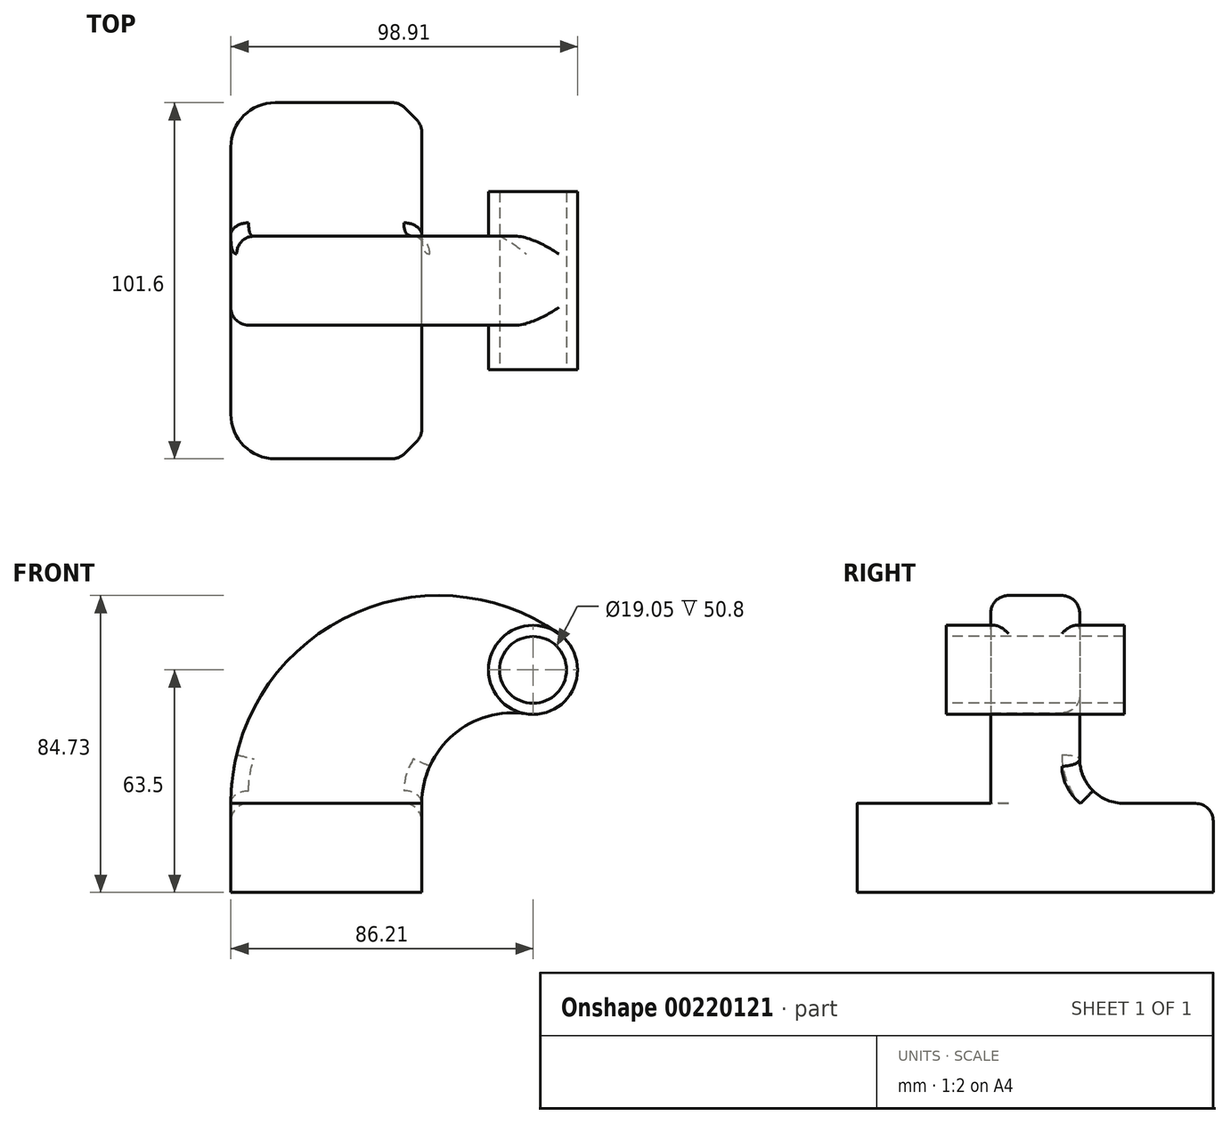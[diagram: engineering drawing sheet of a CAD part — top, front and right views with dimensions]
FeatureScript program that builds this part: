
annotation { "Feature Type Name" : "Feature", "Feature Type Description" : "" }
export const myFeature = defineFeature(function(context is Context, id is Id, definition is map)
    precondition{}
    {
        {
            var Q0;
            Q0=qCreatedBy(makeId("Front.planeOp"),FACE);
            var sketch = newSketch(context, id + "F0", { "sketchPlane" : qUnion([Q0])});
            skLineSegment(sketch, "E0.bottom", {"start": v(-54.46, 0) * mm, "end": v(0, 0) * mm});
            skLineSegment(sketch, "E0.top", {"start": v(-54.46, -25.4) * mm, "end": v(0, -25.4) * mm});
            skLineSegment(sketch, "E0.left", {"start": v(-54.46, 0) * mm, "end": v(-54.46, -25.4) * mm});
            skLineSegment(sketch, "E0.right", {"start": v(0, 0) * mm, "end": v(0, -25.4) * mm});
            skCircle(sketch, "E1", {"center": v(31.75, 38.1) * mm, "radius": 12.7 * mm});
            skArc(sketch, "E2", {"start": v(0, 0) * mm, "mid": v(9.03, 19.63) * mm, "end": v(29.8, 25.55) * mm});
            skArc(sketch, "E3", {"start": v(-54.46, 0) * mm, "mid": v(-22.43, 52.67) * mm, "end": v(39.07, 48.48) * mm});
            skLineSegment(sketch, "E4", {"start": v(39.07, 48.48) * mm, "end": v(39.07, 48.48) * mm});
            skSolve(sketch);
        }
        {
            var Q0;
            Q0=makeQuery(id+"F0.imprint","IMPRINT",FACE,{"disambiguationData":[TD([[makeQuery(id+"F0.imprint","IMPRINT",EDGE,{"derivedFrom":sQuery(id+"F0.wireOp",EDGE,"E0.bottom")}),-1.0]])]});
            extrude(context, id + "F1", {"entities" : qUnion([Q0]), "endBound" : BoundingType.SYMMETRIC, "depth" : 101.6 * mm});
        }
        {
            var Q0;
            Q0=makeQuery(id+"F0.imprint","IMPRINT",FACE,{"disambiguationData":[TD([[makeQuery(id+"F0.imprint","IMPRINT",EDGE,{"derivedFrom":sQuery(id+"F0.wireOp",EDGE,"E0.bottom")}),1.0]])]});
            extrude(context, id + "F2", {"entities" : qUnion([Q0]), "operationType" : NewBodyOperationType.ADD, "endBound" : BoundingType.SYMMETRIC, "depth" : 25.4 * mm});
        }
        {
            var Q0;
            {var subQ0=sQuery(id+"F0.wireOp",EDGE,"E1");var subQ1=makeQuery(id+"F0.imprint","INTERSECT",VERTEX,{"derivedFrom":[subQ0,sQuery(id+"F0.wireOp",EDGE,"E2")]});Q0=makeQuery(id+"F0.imprint","IMPRINT",FACE,{"disambiguationData":[TD([[makeQuery(id+"F0.imprint","IMPRINT",EDGE,{"disambiguationData":[TD([[subQ1,1.0]])],"derivedFrom":subQ0}),1.0]])]});}
            extrude(context, id + "F3", {"entities" : qUnion([Q0]), "operationType" : NewBodyOperationType.ADD, "endBound" : BoundingType.SYMMETRIC, "depth" : 50.8 * mm});
        }
        {
            var Q0;
            Q0=makeQuery(id+"F1.opExtrude","CAP_EDGE",EDGE,{"disambiguationData":[OSD([sQuery(id+"F0.wireOp",EDGE,"E0.right")])],"isStart":false});
            var Q1;
            Q1=makeQuery(id+"F1.opExtrude","CAP_EDGE",EDGE,{"disambiguationData":[OSD([sQuery(id+"F0.wireOp",EDGE,"E0.right")])],"isStart":true});
            chamfer(context, id + "F4", {"entities" : qUnion([Q0, Q1]), "width" : 6.35 * mm, "tangentPropagation" : true});
        }
        {
            var Q0;
            Q0=makeQuery(id+"F1.opExtrude","CAP_EDGE",EDGE,{"disambiguationData":[OSD([sQuery(id+"F0.wireOp",EDGE,"E0.left")])],"isStart":false});
            var Q1;
            Q1=makeQuery(id+"F1.opExtrude","CAP_EDGE",EDGE,{"disambiguationData":[OSD([sQuery(id+"F0.wireOp",EDGE,"E0.left")])],"isStart":true});
            fillet(context, id + "F5", {"entities" : qUnion([Q0, Q1]), "radius" : 12.7 * mm, "tangentPropagation" : true, "allowEdgeOverflow" : false});
        }
        {
            var Q0;
            Q0=makeQuery(id+"F2.opExtrude","CAP_EDGE",EDGE,{"disambiguationData":[OSD([sQuery(id+"F0.wireOp",EDGE,"E0.bottom")])],"isStart":false});
            var Q1;
            Q1=makeQuery(id+"F2.opExtrude","CAP_EDGE",EDGE,{"disambiguationData":[OSD([sQuery(id+"F0.wireOp",EDGE,"E0.bottom")])],"isStart":true});
            fillet(context, id + "F6", {"entities" : qUnion([Q0, Q1]), "radius" : 12.7 * mm, "tangentPropagation" : true, "allowEdgeOverflow" : false});
        }
        {
            var Q0;
            {var subQ0=sQuery(id+"F0.wireOp",EDGE,"E0.right");Q0=makeQuery(id+"F4.opChamfer","BLEND_EDGE",EDGE,{"blendedFrom":[makeQuery(id+"F1.opExtrude","CAP_EDGE",EDGE,{"disambiguationData":[OSD([subQ0])],"isStart":false}),makeQuery(id+"F1.opExtrude","SWEPT_FACE",FACE,{"disambiguationData":[OSD([subQ0])]})],"blendedInto":[makeQuery(id+"F1.opExtrude","SWEPT_FACE",FACE,{"disambiguationData":[OSD([subQ0])]})]});}
            var Q1;
            {var subQ0=sQuery(id+"F0.wireOp",EDGE,"E0.right");Q1=makeQuery(id+"F4.opChamfer","BLEND_EDGE",EDGE,{"blendedFrom":[makeQuery(id+"F1.opExtrude","CAP_EDGE",EDGE,{"disambiguationData":[OSD([subQ0])],"isStart":false}),makeQuery(id+"F1.opExtrude","CAP_FACE",FACE,{"disambiguationData":[OSD([sQuery(id+"F0.wireOp",EDGE,"E0.bottom"),sQuery(id+"F0.wireOp",EDGE,"E0.top"),sQuery(id+"F0.wireOp",EDGE,"E0.left"),subQ0])],"isStart":false})],"blendedInto":[makeQuery(id+"F1.opExtrude","CAP_FACE",FACE,{"disambiguationData":[OSD([sQuery(id+"F0.wireOp",EDGE,"E0.bottom"),sQuery(id+"F0.wireOp",EDGE,"E0.top"),sQuery(id+"F0.wireOp",EDGE,"E0.left"),subQ0])],"isStart":false})]});}
            var Q2;
            {var subQ0=sQuery(id+"F0.wireOp",EDGE,"E0.right");Q2=makeQuery(id+"F4.opChamfer","BLEND_EDGE",EDGE,{"blendedFrom":[makeQuery(id+"F1.opExtrude","CAP_EDGE",EDGE,{"disambiguationData":[OSD([subQ0])],"isStart":true}),makeQuery(id+"F1.opExtrude","SWEPT_FACE",FACE,{"disambiguationData":[OSD([subQ0])]})],"blendedInto":[makeQuery(id+"F1.opExtrude","SWEPT_FACE",FACE,{"disambiguationData":[OSD([subQ0])]})]});}
            var Q3;
            {var subQ0=sQuery(id+"F0.wireOp",EDGE,"E0.right");Q3=makeQuery(id+"F4.opChamfer","BLEND_EDGE",EDGE,{"blendedFrom":[makeQuery(id+"F1.opExtrude","CAP_EDGE",EDGE,{"disambiguationData":[OSD([subQ0])],"isStart":true}),makeQuery(id+"F1.opExtrude","CAP_FACE",FACE,{"disambiguationData":[OSD([sQuery(id+"F0.wireOp",EDGE,"E0.bottom"),sQuery(id+"F0.wireOp",EDGE,"E0.top"),sQuery(id+"F0.wireOp",EDGE,"E0.left"),subQ0])],"isStart":true})],"blendedInto":[makeQuery(id+"F1.opExtrude","CAP_FACE",FACE,{"disambiguationData":[OSD([sQuery(id+"F0.wireOp",EDGE,"E0.bottom"),sQuery(id+"F0.wireOp",EDGE,"E0.top"),sQuery(id+"F0.wireOp",EDGE,"E0.left"),subQ0])],"isStart":true})]});}
            fillet(context, id + "F7", {"entities" : qUnion([Q0, Q1, Q2, Q3]), "radius" : 5.08 * mm, "tangentPropagation" : true, "allowEdgeOverflow" : false});
        }
        {
            var Q0;
            Q0=makeQuery(id+"F2.opExtrude","CAP_EDGE",EDGE,{"disambiguationData":[OSD([sQuery(id+"F0.wireOp",EDGE,"E3")])],"isStart":true});
            var Q1;
            Q1=makeQuery(id+"F2.opExtrude","CAP_EDGE",EDGE,{"disambiguationData":[OSD([sQuery(id+"F0.wireOp",EDGE,"E2")])],"isStart":true});
            var Q2;
            Q2=makeQuery(id+"F6.opFillet","BLEND_EDGE",EDGE,{"blendedFrom":[makeQuery(id+"F2.opExtrude","CAP_EDGE",EDGE,{"disambiguationData":[OSD([sQuery(id+"F0.wireOp",EDGE,"E0.bottom")])],"isStart":true}),makeQuery(id+"F2.opExtrude","SWEPT_FACE",FACE,{"disambiguationData":[OSD([sQuery(id+"F0.wireOp",EDGE,"E2")])]})],"blendedInto":[makeQuery(id+"F2.opExtrude","SWEPT_FACE",FACE,{"disambiguationData":[OSD([sQuery(id+"F0.wireOp",EDGE,"E2")])]})]});
            var Q3;
            {var subQ2=sQuery(id+"F0.wireOp",EDGE,"E0.bottom");var subQ3=sQuery(id+"F0.wireOp",EDGE,"E0.right");var subQ4=sQuery(id+"F0.wireOp",EDGE,"E0.left");Q3=makeQuery(id+"F5.opFillet","BLEND_EDGE",EDGE,{"blendedFrom":[makeQuery(id+"F1.opExtrude","CAP_EDGE",EDGE,{"disambiguationData":[OSD([subQ4])],"isStart":true}),makeQuery(id+"F2.boolean.opBoolean","SPLIT",FACE,{"disambiguationData":[TD([makeQuery(id+"F1.opExtrude","CAP_FACE",FACE,{"disambiguationData":[OSD([subQ2,sQuery(id+"F0.wireOp",EDGE,"E0.top"),subQ4,subQ3])],"isStart":true})])],"derivedFrom":makeQuery(id+"F1.opExtrude","SWEPT_FACE",FACE,{"disambiguationData":[OSD([subQ2])]})})],"blendedInto":[makeQuery(id+"F2.boolean.opBoolean","SPLIT",FACE,{"disambiguationData":[TD([makeQuery(id+"F1.opExtrude","CAP_FACE",FACE,{"disambiguationData":[OSD([subQ2,sQuery(id+"F0.wireOp",EDGE,"E0.top"),subQ4,subQ3])],"isStart":true})])],"derivedFrom":makeQuery(id+"F1.opExtrude","SWEPT_FACE",FACE,{"disambiguationData":[OSD([subQ2])]})})]});}
            var Q4;
            Q4=makeQuery(id+"F1.opExtrude","CAP_EDGE",EDGE,{"disambiguationData":[OSD([sQuery(id+"F0.wireOp",EDGE,"E0.bottom")])],"isStart":true});
            var Q5;
            {var subQ0=sQuery(id+"F0.wireOp",EDGE,"E2");var subQ1=sQuery(id+"F0.wireOp",EDGE,"E0.bottom");var subQ2=sQuery(id+"F0.wireOp",EDGE,"E0.right");Q5=makeQuery(id+"F2.boolean.opBoolean","SPLIT",EDGE,{"disambiguationData":[TD([makeQuery(id+"F1.opExtrude","CAP_FACE",FACE,{"disambiguationData":[OSD([subQ1,sQuery(id+"F0.wireOp",EDGE,"E0.top"),sQuery(id+"F0.wireOp",EDGE,"E0.left"),subQ2])],"isStart":true})])],"derivedFrom":makeQuery(id+"F1.opExtrude","SWEPT_EDGE",EDGE,{"disambiguationData":[OSD([subQ1,subQ2,subQ0])]})});}
            var Q6;
            {var subQ2=sQuery(id+"F0.wireOp",EDGE,"E0.bottom");var subQ3=sQuery(id+"F0.wireOp",EDGE,"E0.right");var subQ4=sQuery(id+"F0.wireOp",EDGE,"E0.left");Q6=makeQuery(id+"F4.opChamfer","BLEND_EDGE",EDGE,{"blendedFrom":[makeQuery(id+"F1.opExtrude","CAP_EDGE",EDGE,{"disambiguationData":[OSD([subQ3])],"isStart":true}),makeQuery(id+"F2.boolean.opBoolean","SPLIT",FACE,{"disambiguationData":[TD([makeQuery(id+"F1.opExtrude","CAP_FACE",FACE,{"disambiguationData":[OSD([subQ2,sQuery(id+"F0.wireOp",EDGE,"E0.top"),subQ4,subQ3])],"isStart":true})])],"derivedFrom":makeQuery(id+"F1.opExtrude","SWEPT_FACE",FACE,{"disambiguationData":[OSD([subQ2])]})})],"blendedInto":[makeQuery(id+"F2.boolean.opBoolean","SPLIT",FACE,{"disambiguationData":[TD([makeQuery(id+"F1.opExtrude","CAP_FACE",FACE,{"disambiguationData":[OSD([subQ2,sQuery(id+"F0.wireOp",EDGE,"E0.top"),subQ4,subQ3])],"isStart":true})])],"derivedFrom":makeQuery(id+"F1.opExtrude","SWEPT_FACE",FACE,{"disambiguationData":[OSD([subQ2])]})})]});}
            var Q7;
            {var subQ2=sQuery(id+"F0.wireOp",EDGE,"E0.bottom");var subQ3=sQuery(id+"F0.wireOp",EDGE,"E0.right");var subQ4=sQuery(id+"F0.wireOp",EDGE,"E0.left");var subQ5=makeQuery(id+"F1.opExtrude","CAP_FACE",FACE,{"disambiguationData":[OSD([subQ2,sQuery(id+"F0.wireOp",EDGE,"E0.top"),subQ4,subQ3])],"isStart":true});Q7=makeQuery(id+"F7.opFillet","BLEND_EDGE",EDGE,{"blendedFrom":[makeQuery(id+"F4.opChamfer","BLEND_EDGE",EDGE,{"blendedFrom":[makeQuery(id+"F1.opExtrude","CAP_EDGE",EDGE,{"disambiguationData":[OSD([subQ3])],"isStart":true}),subQ5],"blendedInto":[subQ5]}),makeQuery(id+"F2.boolean.opBoolean","SPLIT",FACE,{"disambiguationData":[TD([subQ5])],"derivedFrom":makeQuery(id+"F1.opExtrude","SWEPT_FACE",FACE,{"disambiguationData":[OSD([subQ2])]})})],"blendedInto":[makeQuery(id+"F2.boolean.opBoolean","SPLIT",FACE,{"disambiguationData":[TD([subQ5])],"derivedFrom":makeQuery(id+"F1.opExtrude","SWEPT_FACE",FACE,{"disambiguationData":[OSD([subQ2])]})})]});}
            var Q8;
            {var subQ2=sQuery(id+"F0.wireOp",EDGE,"E0.bottom");var subQ3=sQuery(id+"F0.wireOp",EDGE,"E0.right");var subQ4=makeQuery(id+"F1.opExtrude","SWEPT_FACE",FACE,{"disambiguationData":[OSD([subQ3])]});var subQ5=sQuery(id+"F0.wireOp",EDGE,"E0.left");Q8=makeQuery(id+"F7.opFillet","BLEND_EDGE",EDGE,{"blendedFrom":[makeQuery(id+"F4.opChamfer","BLEND_EDGE",EDGE,{"blendedFrom":[makeQuery(id+"F1.opExtrude","CAP_EDGE",EDGE,{"disambiguationData":[OSD([subQ3])],"isStart":true}),subQ4],"blendedInto":[subQ4]}),makeQuery(id+"F2.boolean.opBoolean","SPLIT",FACE,{"disambiguationData":[TD([makeQuery(id+"F1.opExtrude","CAP_FACE",FACE,{"disambiguationData":[OSD([subQ2,sQuery(id+"F0.wireOp",EDGE,"E0.top"),subQ5,subQ3])],"isStart":true})])],"derivedFrom":makeQuery(id+"F1.opExtrude","SWEPT_FACE",FACE,{"disambiguationData":[OSD([subQ2])]})})],"blendedInto":[makeQuery(id+"F2.boolean.opBoolean","SPLIT",FACE,{"disambiguationData":[TD([makeQuery(id+"F1.opExtrude","CAP_FACE",FACE,{"disambiguationData":[OSD([subQ2,sQuery(id+"F0.wireOp",EDGE,"E0.top"),subQ5,subQ3])],"isStart":true})])],"derivedFrom":makeQuery(id+"F1.opExtrude","SWEPT_FACE",FACE,{"disambiguationData":[OSD([subQ2])]})})]});}
            var Q9;
            Q9=makeQuery(id+"F2.opExtrude","CAP_EDGE",EDGE,{"disambiguationData":[OSD([sQuery(id+"F0.wireOp",EDGE,"E3")])],"isStart":false});
            fillet(context, id + "F8", {"entities" : qUnion([Q0, Q1, Q2, Q3, Q4, Q5, Q6, Q7, Q8, Q9]), "radius" : 5.08 * mm, "tangentPropagation" : true, "allowEdgeOverflow" : false});
        }
        {
            var Q0;
            Q0=makeQuery(id+"F3.opExtrude","CAP_FACE",FACE,{"disambiguationData":[OSD([sQuery(id+"F0.wireOp",EDGE,"E1")])],"isStart":false});
            var sketch = newSketch(context, id + "F9", { "sketchPlane" : qUnion([Q0])});
            skPoint(sketch, "E5", {"position": v(31.75, 38.1) * mm});
            skSolve(sketch);
        }
        {
            var Q0;
            Q0=sQuery(id+"F9.wireOp",VERTEX,"E5");
            var Q1;
            Q1=makeQuery(id+"F1.opExtrude","SWEPT_BODY",BODY,{"disambiguationData":[OSD([sQuery(id+"F0.wireOp",EDGE,"E0.bottom"),sQuery(id+"F0.wireOp",EDGE,"E0.top"),sQuery(id+"F0.wireOp",EDGE,"E0.left"),sQuery(id+"F0.wireOp",EDGE,"E0.right")])]});
            hole(context, id + "F10", {"style" : HoleStyle.SIMPLE, "endStyle" : HoleEndStyle.THROUGH, "holeDiameter" : 19.05 * mm, "locations" : qUnion([Q0]), "scope" : qUnion([Q1]), "isTappedThrough" : true});
        }
    });
